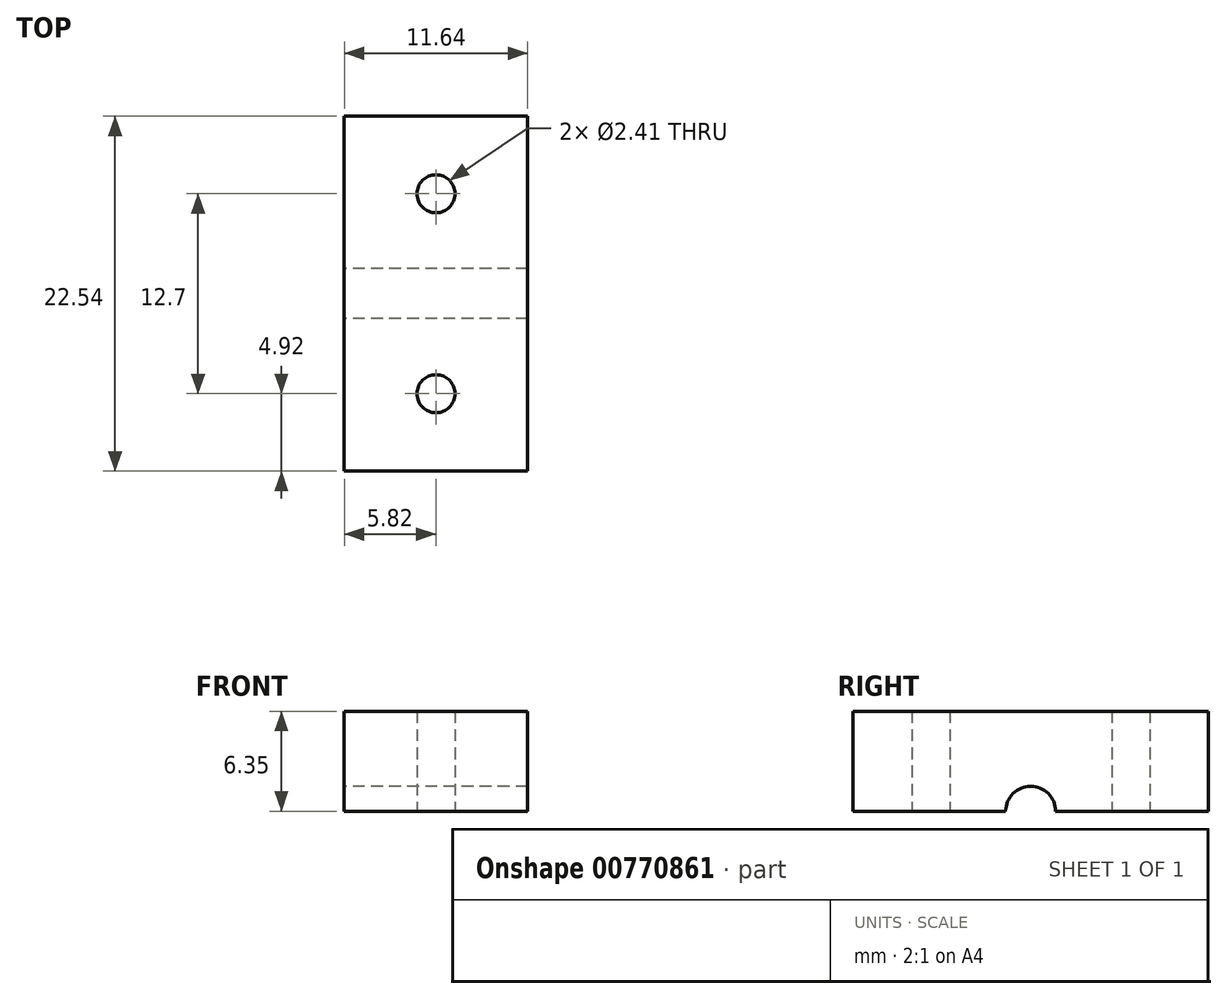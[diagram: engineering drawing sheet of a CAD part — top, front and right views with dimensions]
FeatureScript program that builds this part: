
annotation { "Feature Type Name" : "Feature", "Feature Type Description" : "" }
export const myFeature = defineFeature(function(context is Context, id is Id, definition is map)
    precondition{}
    {
        {
            var Q0;
            Q0=qCreatedBy(makeId("Top.planeOp"),FACE);
            var sketch = newSketch(context, id + "F0", { "sketchPlane" : qUnion([Q0])});
            skLineSegment(sketch, "E0.bottom", {"start": v(5.82, -11.27) * mm, "end": v(-5.82, -11.27) * mm});
            skLineSegment(sketch, "E0.top", {"start": v(5.82, 11.27) * mm, "end": v(-5.82, 11.27) * mm});
            skLineSegment(sketch, "E0.left", {"start": v(5.82, -11.27) * mm, "end": v(5.82, 11.27) * mm});
            skLineSegment(sketch, "E0.right", {"start": v(-5.82, -11.27) * mm, "end": v(-5.82, 11.27) * mm});
            skPoint(sketch, "E0.middle", {"position": v(0, 0) * mm});
            skCircle(sketch, "E1", {"center": v(0, 6.35) * mm, "radius": 1.2 * mm});
            skCircle(sketch, "E2", {"center": v(0, -6.35) * mm, "radius": 1.2 * mm});
            skPoint(sketch, "E3", {"position": v(5.82, -1.59) * mm});
            skPoint(sketch, "E4", {"position": v(5.82, 1.59) * mm});
            skPoint(sketch, "E5", {"position": v(-5.82, -1.59) * mm});
            skPoint(sketch, "E6", {"position": v(-5.82, 1.59) * mm});
            skSolve(sketch);
        }
        {
            var Q0;
            Q0=qCreatedBy(makeId("Right.planeOp"),FACE);
            var sketch = newSketch(context, id + "F1", { "sketchPlane" : qUnion([Q0])});
            skCircle(sketch, "E7", {"center": v(0, 0) * mm, "radius": 1.59 * mm});
            skSolve(sketch);
        }
        {
            var Q0;
            Q0 = qSketchRegion(id + "F0", true);
            extrude(context, id + "F2", {"entities" : qUnion([Q0]), "depth" : 6.35 * mm, "offsetDistance" : 25.4 * mm});
        }
        {
            var Q0;
            Q0=sQuery(id+"F1.wireOp",VERTEX,"E7.center");
            var Q1;
            Q1=makeQuery(id+"F2.opExtrude","SWEPT_BODY",BODY,{"disambiguationData":[OSD([sQuery(id+"F0.wireOp",EDGE,"E0.bottom"),sQuery(id+"F0.wireOp",EDGE,"E0.top"),sQuery(id+"F0.wireOp",EDGE,"E0.left"),sQuery(id+"F0.wireOp",EDGE,"E0.right"),sQuery(id+"F0.wireOp",EDGE,"E1"),sQuery(id+"F0.wireOp",EDGE,"E2")])]});
            hole(context, id + "F3", {"style" : HoleStyle.SIMPLE, "endStyle" : HoleEndStyle.THROUGH, "oppositeDirection" : true, "holeDiameter" : 3.17 * mm, "majorDiameter" : 6.35 * mm, "isTappedThrough" : true, "tappedDepth" : 12.7 * mm, "tapClearance" : 3, "locations" : qUnion([Q0]), "scope" : qUnion([Q1])});
        }
        {
            var Q0;
            Q0=qCreatedBy(makeId("Right.planeOp"),FACE);
            var sketch = newSketch(context, id + "F4", { "sketchPlane" : qUnion([Q0])});
            skCircle(sketch, "E8", {"center": v(0, 0) * mm, "radius": 1.59 * mm});
            skSolve(sketch);
        }
        {
            var Q0;
            Q0=sQuery(id+"F4.wireOp",VERTEX,"E8.center");
            var Q1;
            Q1=makeQuery(id+"F2.opExtrude","SWEPT_BODY",BODY,{"disambiguationData":[OSD([sQuery(id+"F0.wireOp",EDGE,"E0.bottom"),sQuery(id+"F0.wireOp",EDGE,"E0.top"),sQuery(id+"F0.wireOp",EDGE,"E0.left"),sQuery(id+"F0.wireOp",EDGE,"E0.right"),sQuery(id+"F0.wireOp",EDGE,"E1"),sQuery(id+"F0.wireOp",EDGE,"E2")])]});
            hole(context, id + "F5", {"style" : HoleStyle.SIMPLE, "endStyle" : HoleEndStyle.THROUGH, "holeDiameter" : 3.17 * mm, "majorDiameter" : 6.35 * mm, "isTappedThrough" : true, "tappedDepth" : 12.7 * mm, "tapClearance" : 3, "locations" : qUnion([Q0]), "scope" : qUnion([Q1])});
        }
    });
